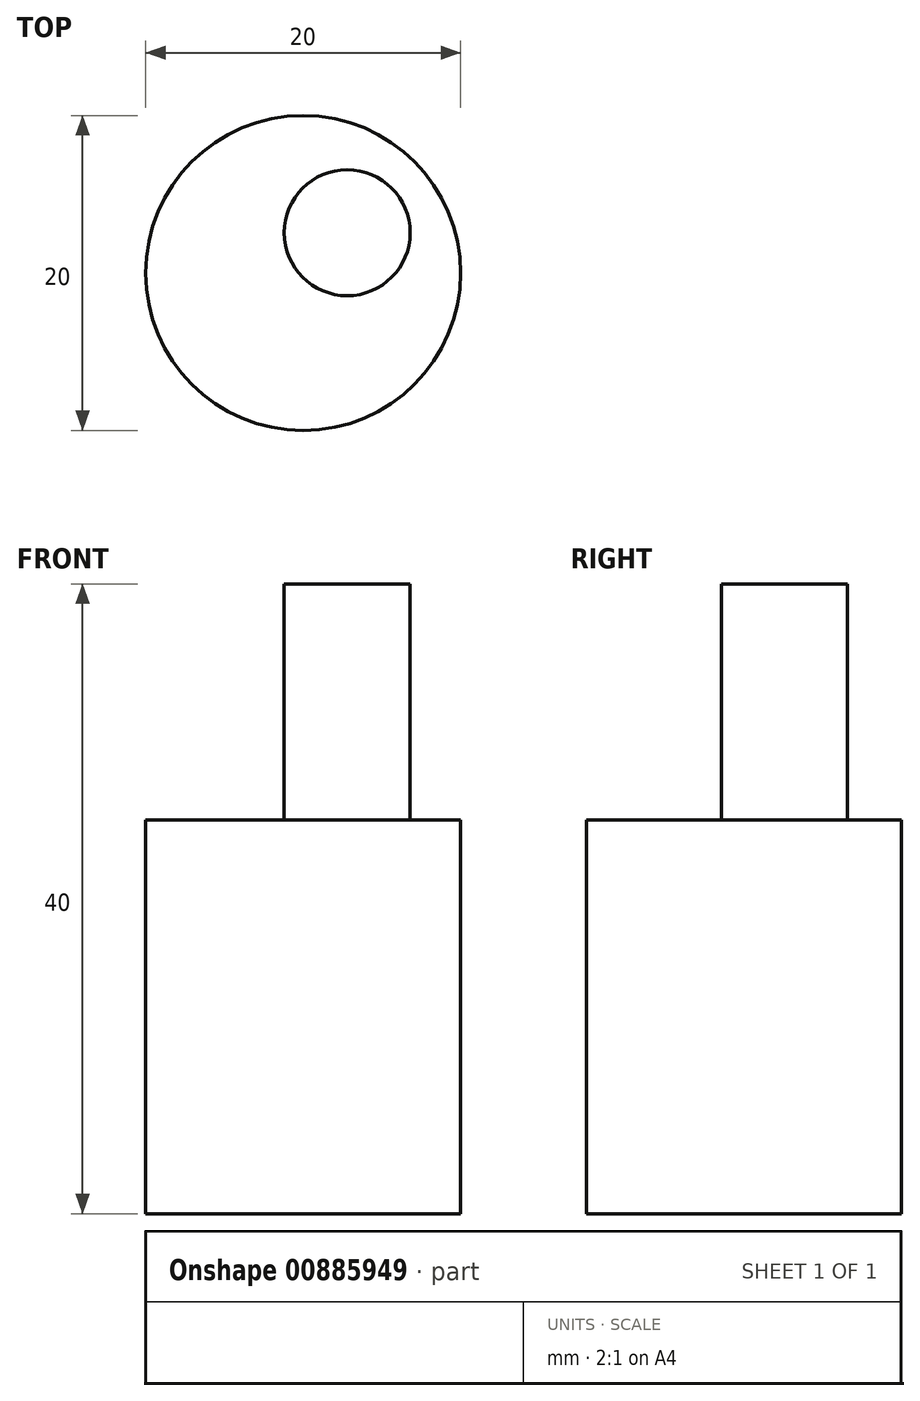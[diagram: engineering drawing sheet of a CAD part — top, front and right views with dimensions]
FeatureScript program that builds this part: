
annotation { "Feature Type Name" : "Feature", "Feature Type Description" : "" }
export const myFeature = defineFeature(function(context is Context, id is Id, definition is map)
    precondition{}
    {
        {
            var Q0;
            Q0=qCreatedBy(makeId("Top.planeOp"),FACE);
            var sketch = newSketch(context, id + "F0", { "sketchPlane" : qUnion([Q0])});
            skCircle(sketch, "E0", {"center": v(0, 0) * mm, "radius": 10 * mm});
            skSolve(sketch);
        }
        {
            var Q0;
            Q0 = qSketchRegion(id + "F0", true);
            extrude(context, id + "F1", {"entities" : qUnion([Q0]), "depth" : 25 * mm, "offsetDistance" : 25 * mm, "symmetric" : true});
        }
        {
            var Q0;
            Q0=makeQuery(id+"F1.opExtrude","CAP_FACE",FACE,{"disambiguationData":[OSD([sQuery(id+"F0.wireOp",EDGE,"E0")])],"isStart":false});
            var sketch = newSketch(context, id + "F2", { "sketchPlane" : qUnion([Q0])});
            skCircle(sketch, "E1", {"center": v(2.8, 2.56) * mm, "radius": 4 * mm});
            skSolve(sketch);
        }
        {
            var Q0;
            Q0=makeQuery(id+"F2.imprint","IMPRINT",FACE,{"disambiguationData":[TD([[makeQuery(id+"F2.imprint","IMPRINT",EDGE,{"derivedFrom":sQuery(id+"F2.wireOp",EDGE,"E1")}),1.0]])]});
            extrude(context, id + "F3", {"entities" : qUnion([Q0]), "operationType" : NewBodyOperationType.ADD, "depth" : 15 * mm, "offsetDistance" : 25 * mm});
        }
    });
